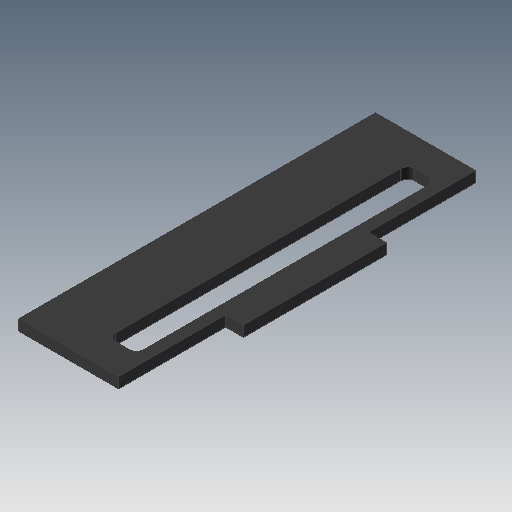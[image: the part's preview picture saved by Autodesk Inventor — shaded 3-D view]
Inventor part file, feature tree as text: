
AUTODESK INVENTOR PART (.ipt)
format: ipt  version: 2020 (Build 240168000, 168)  size: 115,200 bytes
history: native  units: mm
features: extrude x2, sketch x2, fillet x1
ambient origin geometry x8: Origin, YZ Plane, XZ Plane, XY Plane, X Axis, Y Axis, Z Axis, Center Point
bodies: Solid1 (feature_tree)
feature tree (5):
  extrude  "Extrusion1"  Depth=5.0mm
  extrude  "Extrusion4"  Depth=28.0mm
  fillet  "Fillet1"  Radius=3.0mm
  sketch  "Sketch1"  dims[d0=100.0mm d1=5.0mm]
  sketch  "Sketch4"  dims[d2=40.0mm d3=28.0mm d4=3.0mm d5=0.0mm d24=3.0mm d25=8.0mm d26=84.0mm d27=8.0mm d28=10.0mm d29=0.0mm d30=2.0mm]
